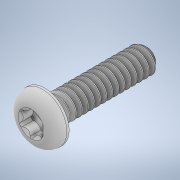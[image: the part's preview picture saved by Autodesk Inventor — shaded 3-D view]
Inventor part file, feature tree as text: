
AUTODESK INVENTOR PART (.ipt)
format: ipt  version: 2021 (Build 250183000, 183)  size: 612,352 bytes
history: native  units: in
note: dims shown in document units (in); Inventor stores cm internally (conversion verified against a paired STEP export)
features: extrude x1
ambient origin geometry x8: Origin, YZ Plane, XZ Plane, XY Plane, X Axis, Y Axis, Z Axis, Center Point
bodies: Solid1 (feature_tree)
feature tree (1):
  extrude  "Extrude16"  [1 undecoded]
note: 1 required parameter value undecoded (feature->parameter linkage not recoverable at this tier; creation-order binding heuristic only, values carry confidence <= 0.55)
